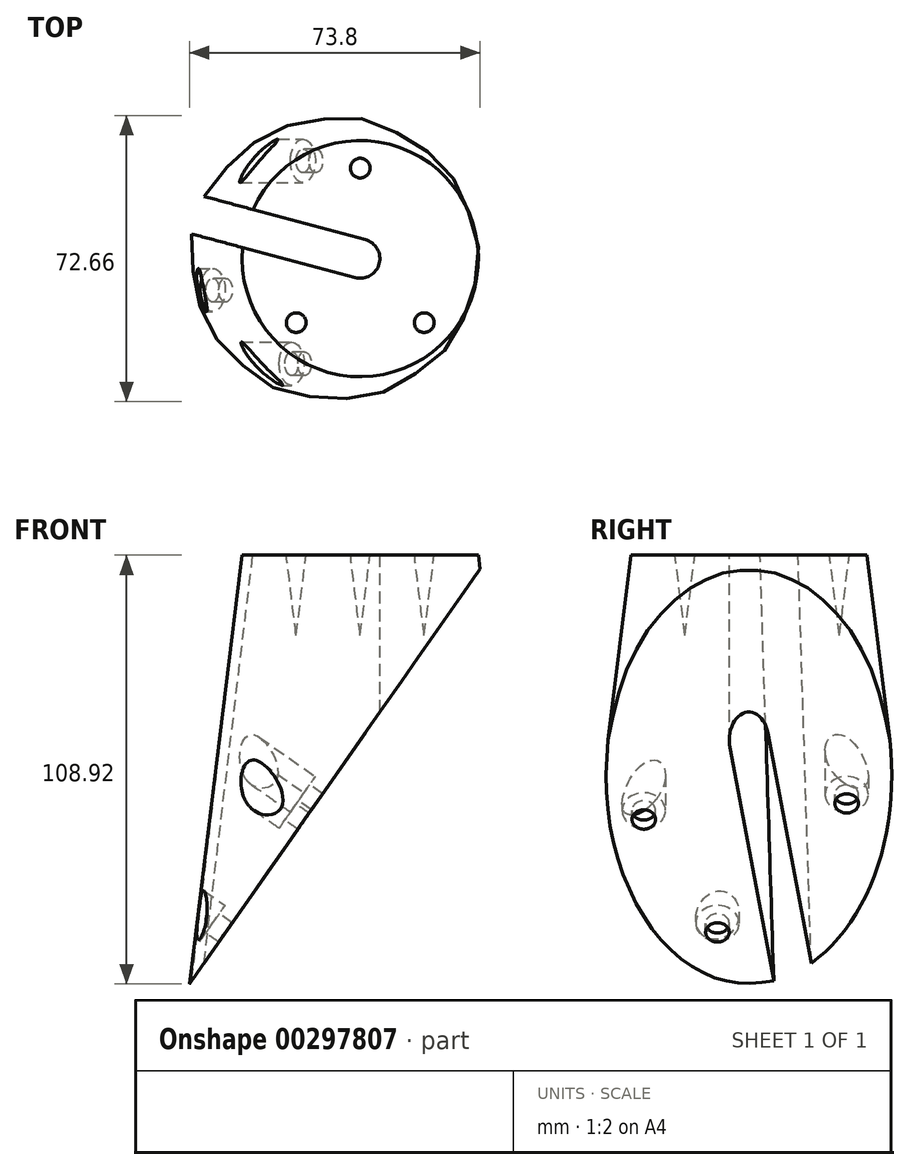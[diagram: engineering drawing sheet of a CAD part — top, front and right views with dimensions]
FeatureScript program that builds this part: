
annotation { "Feature Type Name" : "Feature", "Feature Type Description" : "" }
export const myFeature = defineFeature(function(context is Context, id is Id, definition is map)
    precondition{}
    {
        {
            var Q0;
            Q0=qCreatedBy(makeId("Top.planeOp"),FACE);
            var sketch = newSketch(context, id + "F0", { "sketchPlane" : qUnion([Q0])});
            skCircle(sketch, "E0", {"center": v(0, 0) * mm, "radius": 30 * mm});
            skSolve(sketch);
        }
        {
            var Q0;
            Q0 = qSketchRegion(id + "F0", true);
            extrude(context, id + "F1", {"entities" : qUnion([Q0]), "oppositeDirection" : true, "depth" : 110 * mm, "hasDraft" : true, "draftAngle" : 7 * degree});
        }
        {
            var Q0;
            Q0=qCreatedBy(makeId("Front.planeOp"),FACE);
            var sketch = newSketch(context, id + "F2", { "sketchPlane" : qUnion([Q0])});
            skLineSegment(sketch, "E1", {"start": v(-44.13, -110) * mm, "end": v(45.87, 18.53) * mm});
            skLineSegment(sketch, "E2", {"start": v(45.87, 18.53) * mm, "end": v(45.87, -110) * mm});
            skLineSegment(sketch, "E3", {"start": v(45.87, -110) * mm, "end": v(-44.13, -110) * mm});
            skSolve(sketch);
        }
        {
            var Q0;
            Q0=makeQuery(id+"F2.imprint","IMPRINT",FACE,{"disambiguationData":[TD([[makeQuery(id+"F2.imprint","IMPRINT",EDGE,{"derivedFrom":sQuery(id+"F2.wireOp",EDGE,"E1")}),-1.0]])]});
            extrude(context, id + "F3", {"entities" : qUnion([Q0]), "operationType" : NewBodyOperationType.REMOVE, "oppositeDirection" : true, "depth" : 50 * mm, "hasSecondDirection" : true, "secondDirectionOppositeDirection" : false, "secondDirectionDepth" : 50 * mm});
        }
        {
            var Q0;
            Q0=makeQuery(id+"F1.opExtrude","CAP_FACE",FACE,{"disambiguationData":[OSD([sQuery(id+"F0.wireOp",EDGE,"E0")])],"isStart":true});
            var sketch = newSketch(context, id + "F4", { "sketchPlane" : qUnion([Q0])});
            skCircle(sketch, "E4", {"center": v(0, 0) * mm, "radius": 23 * mm, "construction": true});
            skCircle(sketch, "E5", {"center": v(0, 23) * mm, "radius": 2.5 * mm});
            skLineSegment(sketch, "E6", {"start": v(0, 0) * mm, "end": v(16.26, -16.26) * mm, "construction": true});
            skCircle(sketch, "E7", {"center": v(16.26, -16.26) * mm, "radius": 2.5 * mm});
            skCircle(sketch, "E8.MirrorC", {"center": v(-16.26, -16.26) * mm, "radius": 2.5 * mm});
            skSolve(sketch);
        }
        {
            var Q0;
            Q0 = qSketchRegion(id + "F4", true);
            extrude(context, id + "F5", {"entities" : qUnion([Q0]), "operationType" : NewBodyOperationType.REMOVE, "oppositeDirection" : true, "depth" : 30 * mm, "hasDraft" : true, "draftAngle" : 7 * degree, "draftPullDirection" : true});
        }
        {
            var Q0;
            Q0=makeQuery(id+"F1.opExtrude","CAP_FACE",FACE,{"disambiguationData":[OSD([sQuery(id+"F0.wireOp",EDGE,"E0")])],"isStart":true});
            var sketch = newSketch(context, id + "F6", { "sketchPlane" : qUnion([Q0])});
            skCircle(sketch, "E9", {"center": v(0, 0) * mm, "radius": 5 * mm});
            skLineSegment(sketch, "E10", {"start": v(0, 0) * mm, "end": v(-48.3, 12.94) * mm, "construction": true});
            skCircle(sketch, "E11", {"center": v(-48.3, 12.94) * mm, "radius": 5 * mm});
            skLineSegment(sketch, "E12", {"start": v(-49.6, 8.11) * mm, "end": v(-1.3, -4.83) * mm});
            skLineSegment(sketch, "E13", {"start": v(-47, 17.77) * mm, "end": v(1.3, 4.83) * mm});
            skSolve(sketch);
        }
        {
            var Q0;
            Q0 = qSketchRegion(id + "F6", true);
            extrude(context, id + "F7", {"entities" : qUnion([Q0]), "operationType" : NewBodyOperationType.REMOVE, "oppositeDirection" : true, "depth" : 120 * mm});
        }
        {
            var Q0;
            Q0=makeQuery(id+"F3.boolean.opBoolean","COPY",FACE,{"derivedFrom":makeQuery(id+"F3.opExtrude","SWEPT_FACE",FACE,{"disambiguationData":[OSD([sQuery(id+"F2.wireOp",EDGE,"E1")])]})});
            cPlane(context, id + "F8", {"entities" : qUnion([Q0]), "cplaneType" : CPlaneType.OFFSET, "offset" : 4 * mm, "oppositeDirection" : true, "width" : 150 * mm, "height" : 150 * mm});
        }
        {
            var Q0;
            Q0=qCreatedBy(id+"F8.planeOp",FACE);
            var sketch = newSketch(context, id + "F9", { "sketchPlane" : qUnion([Q0])});
            skCircle(sketch, "E14", {"center": v(-8, -98.13) * mm, "radius": 3 * mm});
            skCircle(sketch, "E15", {"center": v(-26.7, -63.13) * mm, "radius": 3 * mm});
            skCircle(sketch, "E16", {"center": v(24.83, -58.13) * mm, "radius": 3 * mm});
            skSolve(sketch);
        }
        {
            var Q0;
            Q0 = qSketchRegion(id + "F9", true);
            extrude(context, id + "F10", {"entities" : qUnion([Q0]), "operationType" : NewBodyOperationType.REMOVE, "depth" : 70 * mm, "hasSecondDirection" : true, "secondDirectionOppositeDirection" : true, "secondDirectionDepth" : 70 * mm});
        }
        {
            var Q0;
            Q0=qCreatedBy(id+"F8.planeOp",FACE);
            var sketch = newSketch(context, id + "F11", { "sketchPlane" : qUnion([Q0])});
            skCircle(sketch, "E17", {"center": v(24.83, -58.13) * mm, "radius": 5.5 * mm});
            skCircle(sketch, "E18", {"center": v(-26.7, -63.13) * mm, "radius": 5.5 * mm});
            skCircle(sketch, "E19", {"center": v(-8, -98.13) * mm, "radius": 5.5 * mm});
            skSolve(sketch);
        }
        {
            var Q0;
            Q0 = qSketchRegion(id + "F11", true);
            extrude(context, id + "F12", {"entities" : qUnion([Q0]), "operationType" : NewBodyOperationType.REMOVE, "oppositeDirection" : true, "depth" : 45 * mm});
        }
    });
